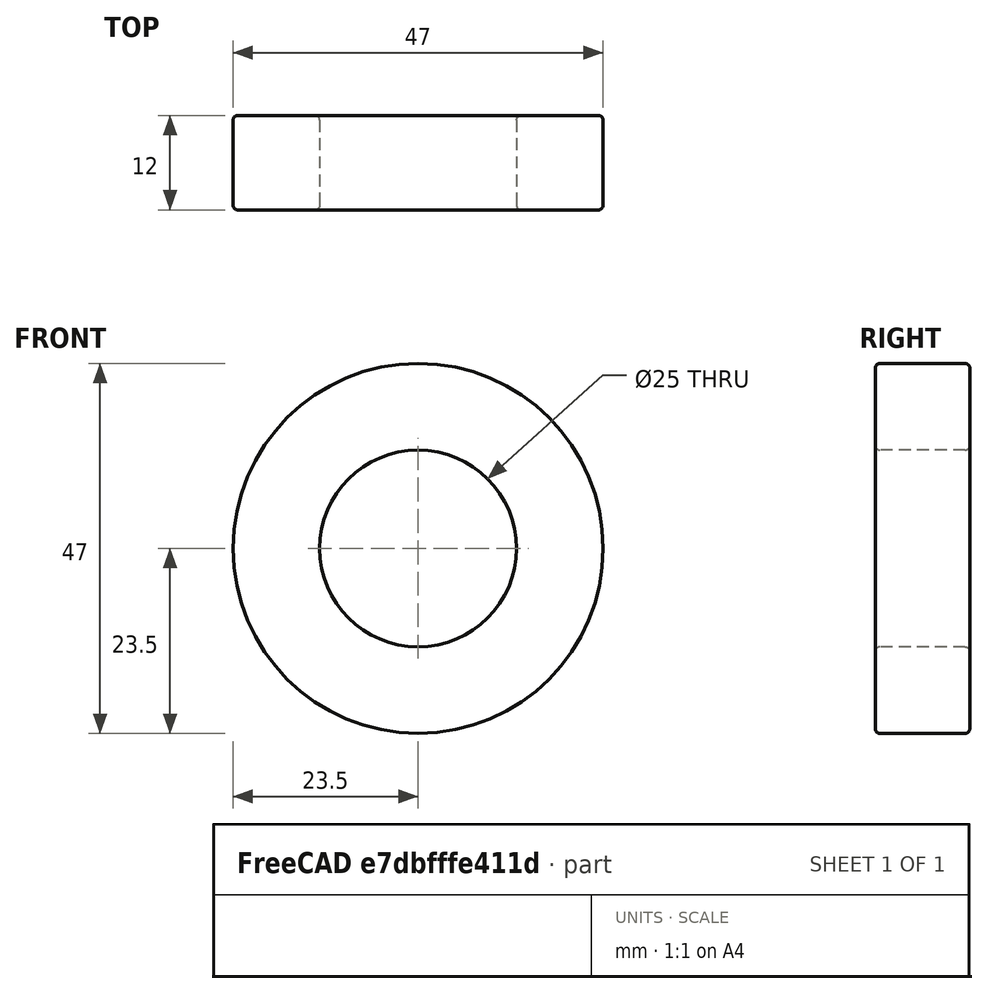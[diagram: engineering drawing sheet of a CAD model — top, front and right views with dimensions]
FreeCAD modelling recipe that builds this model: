
FCSTD DOCUMENT  (FreeCAD 0.20R29126 (Git))
Label: electric-motor-roller-bearing
License: All rights reserved
LicenseURL: http://en.wikipedia.org/wiki/All_rights_reserved
objects: Sketcher::SketchObject×1, PartDesign::Revolution×1, PartDesign::Body×1
note: 4 computed .brp shape members not serialized (recipe doc carries the construction recipe); baked Part::Feature solids carry a one-line shape summary decoded from their .brp

FEATURE [Sketcher::SketchObject] Sketch
  FullyConstrained = true
  MapMode = 5
  Placement = pos=(0,0,0) rot=(0.57735,0.57735,0.57735;2.0944rad)
  Support = -> [YZ_Plane]
  sketch-geometry (10):
    g0: ArcOfCircle CenterX=-5.4 CenterY=22.9 CenterZ=0 NormalX=0 NormalY=0 NormalZ=1 AngleXU=0 Radius=0.6 StartAngle=1.5708 EndAngle=3.14159
    g1: LineSegment StartX=-5.4 StartY=23.5 StartZ=0 EndX=5.4 EndY=23.5 EndZ=0
    g2: ArcOfCircle CenterX=5.4 CenterY=22.9 CenterZ=0 NormalX=0 NormalY=0 NormalZ=1 AngleXU=0 Radius=0.6 StartAngle=3.1e-15 EndAngle=1.5708
    g3: LineSegment StartX=6 StartY=22.9 StartZ=0 EndX=6 EndY=13.1 EndZ=0
    g4: ArcOfCircle CenterX=5.4 CenterY=13.1 CenterZ=0 NormalX=0 NormalY=0 NormalZ=1 AngleXU=0 Radius=0.6 StartAngle=4.71239 EndAngle=6.28319
    g5: LineSegment StartX=5.4 StartY=12.5 StartZ=0 EndX=-5.4 EndY=12.5 EndZ=0
    g6: ArcOfCircle CenterX=-5.4 CenterY=13.1 CenterZ=0 NormalX=0 NormalY=0 NormalZ=1 AngleXU=0 Radius=0.6 StartAngle=3.14159 EndAngle=4.71239
    g7: LineSegment StartX=-6 StartY=13.1 StartZ=0 EndX=-6 EndY=22.9 EndZ=0
    g8: GeomPoint X=-6 Y=23.5 Z=0
    g9: GeomPoint X=6 Y=12.5 Z=0
  constraints (23):
    c: Tangent(g0,g1) = 1.5708
    c: Tangent(g1,g2) = 1.5708
    c: Tangent(g2,g3) = 1.5708
    c: Tangent(g3,g4) = 1.5708
    c: Tangent(g4,g5) = 1.5708
    c: Tangent(g5,g6) = 1.5708
    c: Tangent(g6,g7) = 1.5708
    c: Tangent(g7,g0) = 1.5708
    c: Horizontal(g5)
    c: Vertical(g3)
    c: Vertical(g7)
    c: Equal(g0,g2)
    c: Equal(g2,g4)
    c: Equal(g4,g6)
    c: PointOnObject(g8,g1)
    c: PointOnObject(g8,g7)
    c: PointOnObject(g9,g3)
    c: PointOnObject(g9,g5)
    c: DistanceY(g-1,g4) = 12.5
    c: Radius(g4) = 0.6
    c: DistanceY(g-1,g1) = 23.5
    c: Symmetric(g0,g1,g-2)
    c: DistanceX(g0,g2) = 12
FEATURE [PartDesign::Revolution] Revolution
  Angle = 360
  Axis = (1e-16,1,-1e-16)
  Base = (0,0,0)
  Placement = pos=(0,0,0) rot=(0.57735,0.57735,0.57735;2.0944rad)
  Profile = -> Sketch
  ReferenceAxis = -> Y_Axis
FEATURE [PartDesign::Body] Body
  Group = -> [Sketch,Revolution]
  Origin = -> Origin
  Tip = -> Revolution
